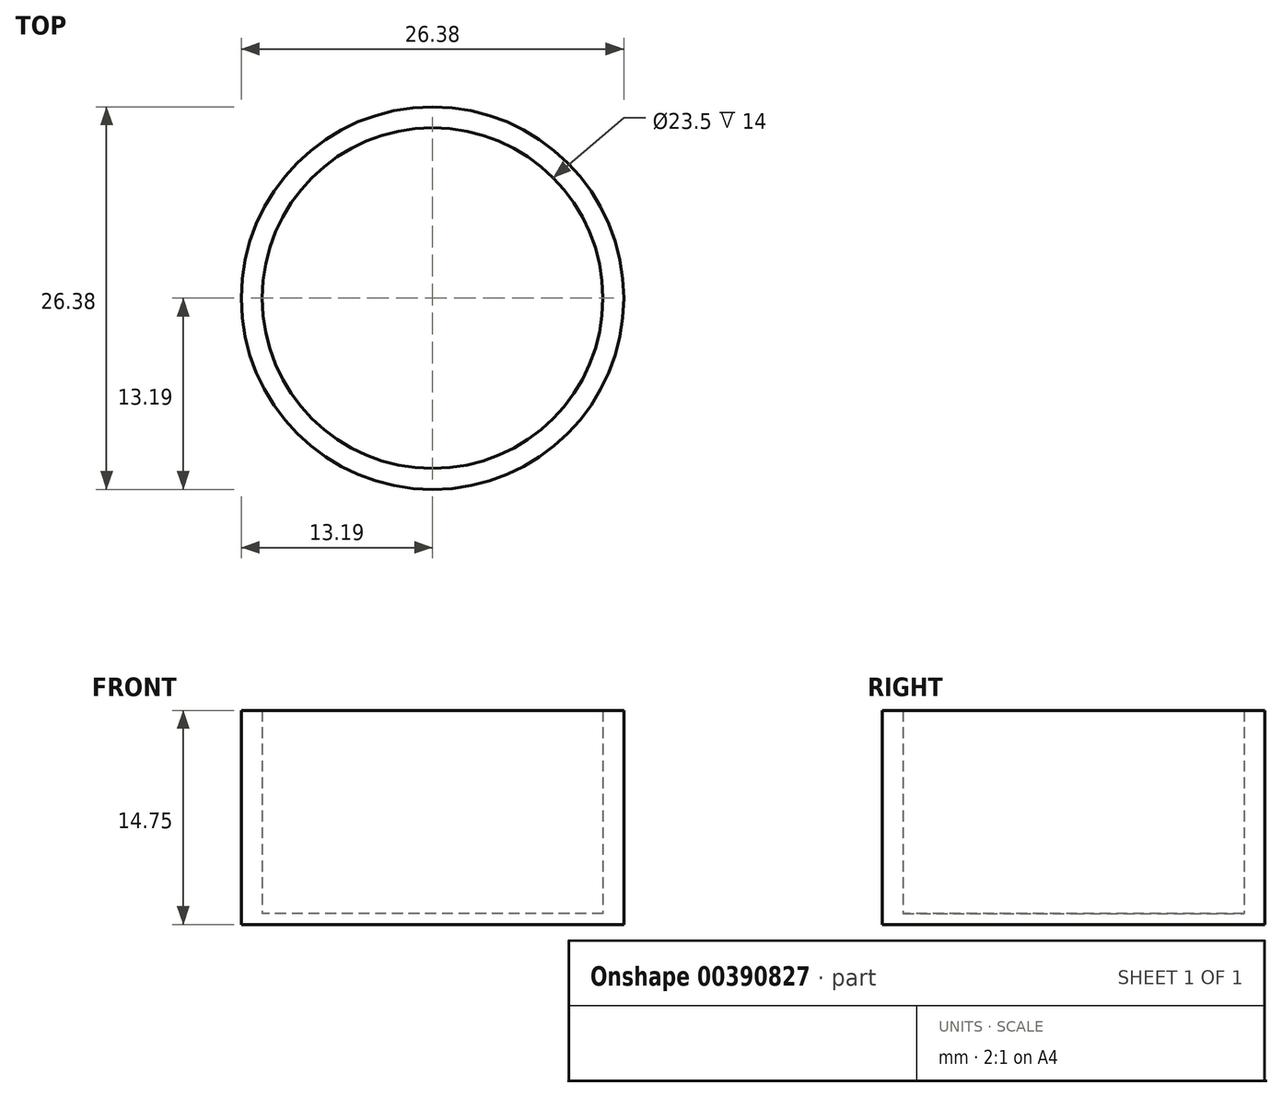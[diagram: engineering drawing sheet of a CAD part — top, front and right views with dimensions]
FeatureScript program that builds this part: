
annotation { "Feature Type Name" : "Feature", "Feature Type Description" : "" }
export const myFeature = defineFeature(function(context is Context, id is Id, definition is map)
    precondition{}
    {
        {
            var Q0;
            Q0=qCreatedBy(makeId("Top.planeOp"),FACE);
            var sketch = newSketch(context, id + "F0", { "sketchPlane" : qUnion([Q0])});
            skCircle(sketch, "E0", {"center": v(0, 0) * mm, "radius": 13.2 * mm});
            skSolve(sketch);
        }
        {
            var Q0;
            Q0 = qSketchRegion(id + "F0", true);
            extrude(context, id + "F1", {"entities" : qUnion([Q0]), "depth" : .75 * mm});
        }
        {
            var Q0;
            Q0=makeQuery(id+"F1.opExtrude","CAP_FACE",FACE,{"disambiguationData":[OSD([sQuery(id+"F0.wireOp",EDGE,"E0")])],"isStart":false});
            var sketch = newSketch(context, id + "F2", { "sketchPlane" : qUnion([Q0])});
            skCircle(sketch, "E1.0.0", {"center": v(0, 0) * mm, "radius": 13.2 * mm});
            skCircle(sketch, "E2.0", {"center": v(0, 0) * mm, "radius": 11.75 * mm});
            skSolve(sketch);
        }
        {
            var Q0;
            Q0 = qSketchRegion(id + "F2", true);
            extrude(context, id + "F3", {"entities" : qUnion([Q0]), "operationType" : NewBodyOperationType.ADD, "depth" : 14 * mm});
        }
    });
